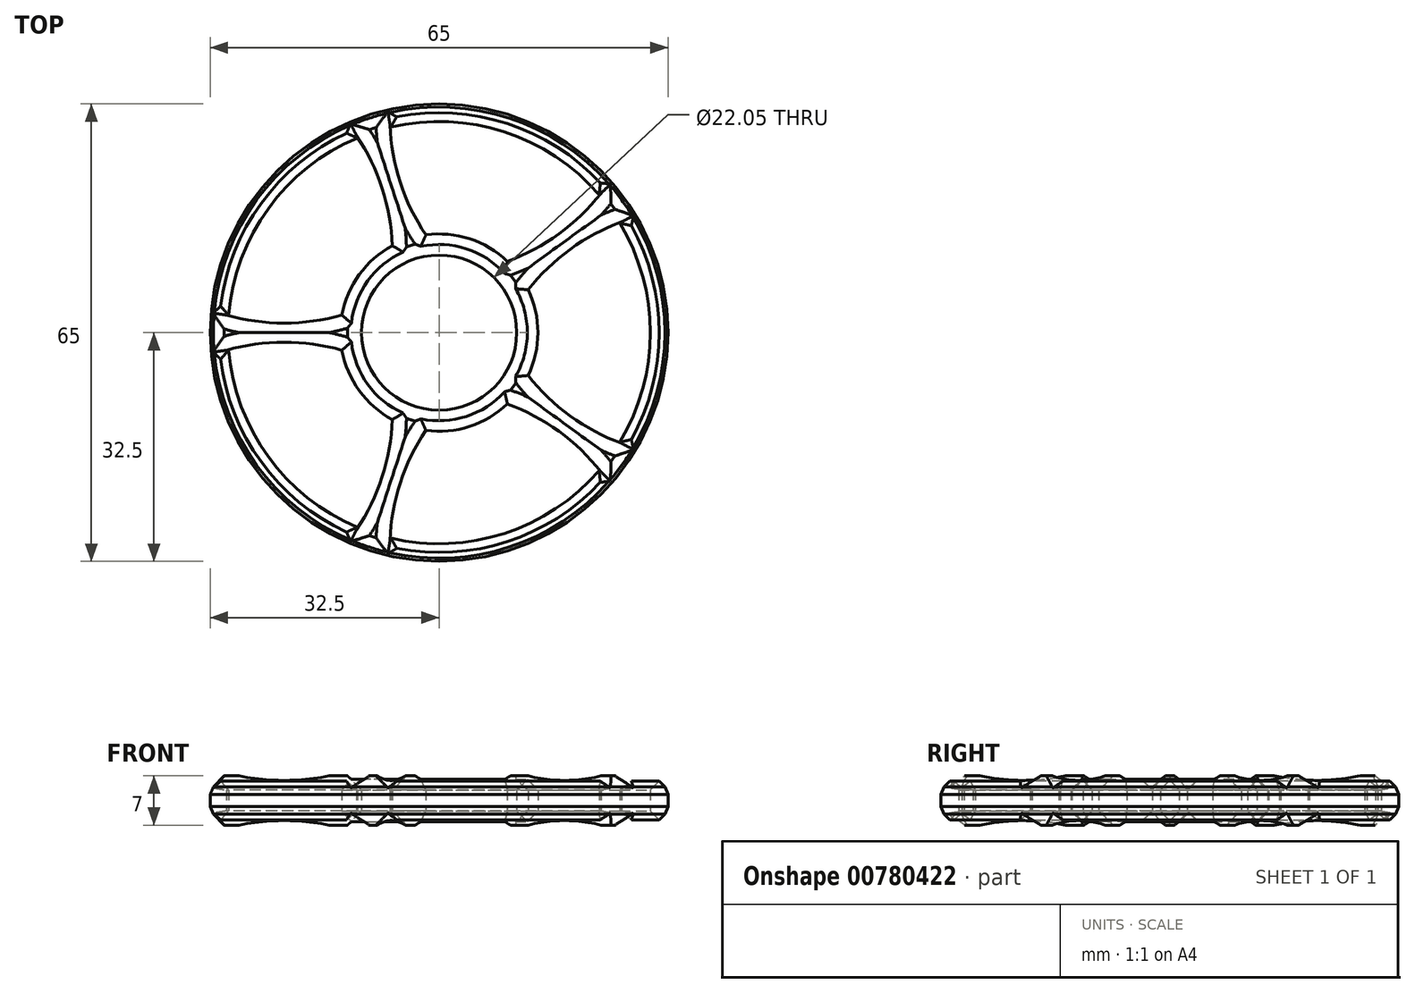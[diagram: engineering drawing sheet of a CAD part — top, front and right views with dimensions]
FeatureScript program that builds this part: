
annotation { "Feature Type Name" : "Feature", "Feature Type Description" : "" }
export const myFeature = defineFeature(function(context is Context, id is Id, definition is map)
    precondition{}
    {
        {
            var Q0;
            Q0=qCreatedBy(makeId("Top.planeOp"),FACE);
            var sketch = newSketch(context, id + "F0", { "sketchPlane" : qUnion([Q0])});
            skCircle(sketch, "E0", {"center": v(0, 0) * mm, "radius": 11.03 * mm});
            skCircle(sketch, "E1.0", {"center": v(0, 0) * mm, "radius": 14.02 * mm});
            skCircle(sketch, "E2", {"center": v(0, 0) * mm, "radius": 30 * mm});
            skLineSegment(sketch, "E3", {"start": v(-14.02, 0) * mm, "end": v(-30, 0) * mm});
            skCircle(sketch, "E4", {"center": v(0, 0) * mm, "radius": 32.5 * mm});
            skLineSegment(sketch, "E5.bottom", {"start": v(-13.8, -2.5) * mm, "end": v(-30.22, -2.5) * mm});
            skLineSegment(sketch, "E5.top", {"start": v(-13.8, 2.5) * mm, "end": v(-30.22, 2.5) * mm});
            skLineSegment(sketch, "E5.left", {"start": v(-13.8, -2.5) * mm, "end": v(-13.8, 2.5) * mm});
            skLineSegment(sketch, "E5.right", {"start": v(-30.22, -2.5) * mm, "end": v(-30.22, 2.5) * mm});
            skPoint(sketch, "E5.middle", {"position": v(-22.01, 0) * mm});
            skArc(sketch, "E6", {"start": v(-30.22, 2.5) * mm, "mid": v(-22.01, 1.35) * mm, "end": v(-13.8, 2.5) * mm});
            skArc(sketch, "E7", {"start": v(-13.8, -2.5) * mm, "mid": v(-22.01, -1.35) * mm, "end": v(-30.22, -2.5) * mm});
            skLineSegment(sketch, "E8.1.0", {"start": v(-6.64, -12.35) * mm, "end": v(-11.72, -27.97) * mm});
            skArc(sketch, "E8.1.1", {"start": v(-11.72, -27.97) * mm, "mid": v(-8.09, -20.52) * mm, "end": v(-6.64, -12.35) * mm});
            skLineSegment(sketch, "E8.1.2", {"start": v(-4.33, -13.34) * mm, "end": v(-9.27, -28.53) * mm});
            skArc(sketch, "E8.1.3", {"start": v(-1.89, -13.9) * mm, "mid": v(-5.51, -21.35) * mm, "end": v(-6.96, -29.52) * mm});
            skLineSegment(sketch, "E8.1.4", {"start": v(-1.89, -13.9) * mm, "end": v(-6.96, -29.52) * mm});
            skLineSegment(sketch, "E8.2.0", {"start": v(9.7, -10.13) * mm, "end": v(22.98, -19.79) * mm});
            skArc(sketch, "E8.2.1", {"start": v(22.98, -19.79) * mm, "mid": v(17.01, -14.03) * mm, "end": v(9.7, -10.13) * mm});
            skLineSegment(sketch, "E8.2.2", {"start": v(11.35, -8.24) * mm, "end": v(24.27, -17.63) * mm});
            skArc(sketch, "E8.2.3", {"start": v(12.63, -6.09) * mm, "mid": v(18.6, -11.84) * mm, "end": v(25.92, -15.74) * mm});
            skLineSegment(sketch, "E8.2.4", {"start": v(12.63, -6.09) * mm, "end": v(25.92, -15.74) * mm});
            skLineSegment(sketch, "E8.3.0", {"start": v(12.63, 6.09) * mm, "end": v(25.92, 15.74) * mm});
            skArc(sketch, "E8.3.1", {"start": v(25.92, 15.74) * mm, "mid": v(18.6, 11.84) * mm, "end": v(12.63, 6.09) * mm});
            skLineSegment(sketch, "E8.3.2", {"start": v(11.35, 8.24) * mm, "end": v(24.27, 17.63) * mm});
            skArc(sketch, "E8.3.3", {"start": v(9.7, 10.13) * mm, "mid": v(17.01, 14.03) * mm, "end": v(22.98, 19.79) * mm});
            skLineSegment(sketch, "E8.3.4", {"start": v(9.7, 10.13) * mm, "end": v(22.98, 19.79) * mm});
            skLineSegment(sketch, "E8.4.0", {"start": v(-1.89, 13.9) * mm, "end": v(-6.96, 29.52) * mm});
            skArc(sketch, "E8.4.1", {"start": v(-6.96, 29.52) * mm, "mid": v(-5.51, 21.35) * mm, "end": v(-1.89, 13.9) * mm});
            skLineSegment(sketch, "E8.4.2", {"start": v(-4.33, 13.34) * mm, "end": v(-9.27, 28.53) * mm});
            skArc(sketch, "E8.4.3", {"start": v(-6.64, 12.35) * mm, "mid": v(-8.09, 20.52) * mm, "end": v(-11.72, 27.97) * mm});
            skLineSegment(sketch, "E8.4.4", {"start": v(-6.64, 12.35) * mm, "end": v(-11.72, 27.97) * mm});
            skSolve(sketch);
        }
        {
            var Q0;
            Q0=makeQuery(id+"F0.imprint","IMPRINT",FACE,{"disambiguationData":[TD([[makeQuery(id+"F0.imprint","IMPRINT",EDGE,{"derivedFrom":sQuery(id+"F0.wireOp",EDGE,"E4")}),1.0]])]});
            var Q1;
            {var subQ3=sQuery(id+"F0.wireOp",EDGE,"E8.1.2");Q1=makeQuery(id+"F0.imprint","IMPRINT",FACE,{"disambiguationData":[TD([[makeQuery(id+"F0.imprint","IMPRINT",EDGE,{"derivedFrom":subQ3}),-1.0]])]});}
            var Q2;
            {var subQ0=sQuery(id+"F0.wireOp",EDGE,"E8.1.2");Q2=makeQuery(id+"F0.imprint","IMPRINT",FACE,{"disambiguationData":[TD([[makeQuery(id+"F0.imprint","IMPRINT",EDGE,{"derivedFrom":subQ0}),1.0]])]});}
            var Q3;
            {var subQ3=sQuery(id+"F0.wireOp",EDGE,"E8.2.2");Q3=makeQuery(id+"F0.imprint","IMPRINT",FACE,{"disambiguationData":[TD([[makeQuery(id+"F0.imprint","IMPRINT",EDGE,{"derivedFrom":subQ3}),-1.0]])]});}
            var Q4;
            {var subQ0=sQuery(id+"F0.wireOp",EDGE,"E8.2.2");Q4=makeQuery(id+"F0.imprint","IMPRINT",FACE,{"disambiguationData":[TD([[makeQuery(id+"F0.imprint","IMPRINT",EDGE,{"derivedFrom":subQ0}),1.0]])]});}
            var Q5;
            {var subQ3=sQuery(id+"F0.wireOp",EDGE,"E8.3.2");Q5=makeQuery(id+"F0.imprint","IMPRINT",FACE,{"disambiguationData":[TD([[makeQuery(id+"F0.imprint","IMPRINT",EDGE,{"derivedFrom":subQ3}),-1.0]])]});}
            var Q6;
            {var subQ0=sQuery(id+"F0.wireOp",EDGE,"E8.3.2");Q6=makeQuery(id+"F0.imprint","IMPRINT",FACE,{"disambiguationData":[TD([[makeQuery(id+"F0.imprint","IMPRINT",EDGE,{"derivedFrom":subQ0}),1.0]])]});}
            var Q7;
            {var subQ0=sQuery(id+"F0.wireOp",EDGE,"E8.4.2");Q7=makeQuery(id+"F0.imprint","IMPRINT",FACE,{"disambiguationData":[TD([[makeQuery(id+"F0.imprint","IMPRINT",EDGE,{"derivedFrom":subQ0}),1.0]])]});}
            var Q8;
            {var subQ3=sQuery(id+"F0.wireOp",EDGE,"E8.4.2");Q8=makeQuery(id+"F0.imprint","IMPRINT",FACE,{"disambiguationData":[TD([[makeQuery(id+"F0.imprint","IMPRINT",EDGE,{"derivedFrom":subQ3}),-1.0]])]});}
            var Q9;
            {var subQ3=sQuery(id+"F0.wireOp",EDGE,"E8.5.2");Q9=makeQuery(id+"F0.imprint","IMPRINT",FACE,{"disambiguationData":[TD([[makeQuery(id+"F0.imprint","IMPRINT",EDGE,{"derivedFrom":subQ3}),-1.0]])]});}
            var Q10;
            {var subQ0=sQuery(id+"F0.wireOp",EDGE,"E8.5.2");Q10=makeQuery(id+"F0.imprint","IMPRINT",FACE,{"disambiguationData":[TD([[makeQuery(id+"F0.imprint","IMPRINT",EDGE,{"derivedFrom":subQ0}),1.0]])]});}
            var Q11;
            Q11=makeQuery(id+"F0.imprint","IMPRINT",FACE,{"disambiguationData":[TD([[makeQuery(id+"F0.imprint","IMPRINT",EDGE,{"derivedFrom":sQuery(id+"F0.wireOp",EDGE,"E0")}),-1.0]])]});
            var Q12;
            {var subQ3=sQuery(id+"F0.wireOp",EDGE,"E8.6.2");Q12=makeQuery(id+"F0.imprint","IMPRINT",FACE,{"disambiguationData":[TD([[makeQuery(id+"F0.imprint","IMPRINT",EDGE,{"derivedFrom":subQ3}),-1.0]])]});}
            var Q13;
            {var subQ0=sQuery(id+"F0.wireOp",EDGE,"E8.6.2");Q13=makeQuery(id+"F0.imprint","IMPRINT",FACE,{"disambiguationData":[TD([[makeQuery(id+"F0.imprint","IMPRINT",EDGE,{"derivedFrom":subQ0}),1.0]])]});}
            var Q14;
            {var subQ0=sQuery(id+"F0.wireOp",EDGE,"E3");Q14=makeQuery(id+"F0.imprint","IMPRINT",FACE,{"disambiguationData":[TD([[makeQuery(id+"F0.imprint","IMPRINT",EDGE,{"derivedFrom":subQ0}),-1.0]])]});}
            var Q15;
            {var subQ0=sQuery(id+"F0.wireOp",EDGE,"E3");Q15=makeQuery(id+"F0.imprint","IMPRINT",FACE,{"disambiguationData":[TD([[makeQuery(id+"F0.imprint","IMPRINT",EDGE,{"derivedFrom":subQ0}),1.0]])]});}
            var Q16;
            {var subQ2=sQuery(id+"F0.wireOp",EDGE,"E5.left");Q16=makeQuery(id+"F0.imprint","IMPRINT",FACE,{"disambiguationData":[TD([[makeQuery(id+"F0.imprint","IMPRINT",EDGE,{"derivedFrom":subQ2}),1.0]])]});}
            var Q17;
            {var subQ1=sQuery(id+"F0.wireOp",EDGE,"E5.right");Q17=makeQuery(id+"F0.imprint","IMPRINT",FACE,{"disambiguationData":[TD([[makeQuery(id+"F0.imprint","IMPRINT",EDGE,{"derivedFrom":subQ1}),-1.0]])]});}
            extrude(context, id + "F1", {"entities" : qUnion([Q0, Q1, Q2, Q3, Q4, Q5, Q6, Q7, Q8, Q9, Q10, Q11, Q12, Q13, Q14, Q15, Q16, Q17]), "depth" : 7 * mm, "offsetDistance" : 25 * mm});
        }
        {
            var Q0;
            Q0=makeQuery(id+"F1.opExtrude","CAP_FACE",FACE,{"disambiguationData":[OSD([sQuery(id+"F0.wireOp",EDGE,"E0"),sQuery(id+"F0.wireOp",EDGE,"E1.0"),sQuery(id+"F0.wireOp",EDGE,"E2"),sQuery(id+"F0.wireOp",EDGE,"E4"),sQuery(id+"F0.wireOp",EDGE,"E5.bottom"),sQuery(id+"F0.wireOp",EDGE,"E5.top"),sQuery(id+"F0.wireOp",EDGE,"E6"),sQuery(id+"F0.wireOp",EDGE,"E7"),sQuery(id+"F0.wireOp",EDGE,"E8.1.0"),sQuery(id+"F0.wireOp",EDGE,"E8.1.1"),sQuery(id+"F0.wireOp",EDGE,"E8.1.3"),sQuery(id+"F0.wireOp",EDGE,"E8.1.4"),sQuery(id+"F0.wireOp",EDGE,"E8.2.0"),sQuery(id+"F0.wireOp",EDGE,"E8.2.1"),sQuery(id+"F0.wireOp",EDGE,"E8.2.3"),sQuery(id+"F0.wireOp",EDGE,"E8.2.4"),sQuery(id+"F0.wireOp",EDGE,"E8.3.0"),sQuery(id+"F0.wireOp",EDGE,"E8.3.1"),sQuery(id+"F0.wireOp",EDGE,"E8.3.3"),sQuery(id+"F0.wireOp",EDGE,"E8.3.4"),sQuery(id+"F0.wireOp",EDGE,"E8.4.0"),sQuery(id+"F0.wireOp",EDGE,"E8.4.1"),sQuery(id+"F0.wireOp",EDGE,"E8.4.3"),sQuery(id+"F0.wireOp",EDGE,"E8.4.4"),sQuery(id+"F0.wireOp",EDGE,"E8.5.0"),sQuery(id+"F0.wireOp",EDGE,"E8.5.1"),sQuery(id+"F0.wireOp",EDGE,"E8.5.3"),sQuery(id+"F0.wireOp",EDGE,"E8.5.4"),sQuery(id+"F0.wireOp",EDGE,"E8.6.0"),sQuery(id+"F0.wireOp",EDGE,"E8.6.1"),sQuery(id+"F0.wireOp",EDGE,"E8.6.3"),sQuery(id+"F0.wireOp",EDGE,"E8.6.4")])],"isStart":false});
            var Q1;
            Q1=makeQuery(id+"F1.opExtrude","CAP_FACE",FACE,{"disambiguationData":[OSD([sQuery(id+"F0.wireOp",EDGE,"E0"),sQuery(id+"F0.wireOp",EDGE,"E1.0"),sQuery(id+"F0.wireOp",EDGE,"E2"),sQuery(id+"F0.wireOp",EDGE,"E4"),sQuery(id+"F0.wireOp",EDGE,"E5.bottom"),sQuery(id+"F0.wireOp",EDGE,"E5.top"),sQuery(id+"F0.wireOp",EDGE,"E6"),sQuery(id+"F0.wireOp",EDGE,"E7"),sQuery(id+"F0.wireOp",EDGE,"E8.1.0"),sQuery(id+"F0.wireOp",EDGE,"E8.1.1"),sQuery(id+"F0.wireOp",EDGE,"E8.1.3"),sQuery(id+"F0.wireOp",EDGE,"E8.1.4"),sQuery(id+"F0.wireOp",EDGE,"E8.2.0"),sQuery(id+"F0.wireOp",EDGE,"E8.2.1"),sQuery(id+"F0.wireOp",EDGE,"E8.2.3"),sQuery(id+"F0.wireOp",EDGE,"E8.2.4"),sQuery(id+"F0.wireOp",EDGE,"E8.3.0"),sQuery(id+"F0.wireOp",EDGE,"E8.3.1"),sQuery(id+"F0.wireOp",EDGE,"E8.3.3"),sQuery(id+"F0.wireOp",EDGE,"E8.3.4"),sQuery(id+"F0.wireOp",EDGE,"E8.4.0"),sQuery(id+"F0.wireOp",EDGE,"E8.4.1"),sQuery(id+"F0.wireOp",EDGE,"E8.4.3"),sQuery(id+"F0.wireOp",EDGE,"E8.4.4"),sQuery(id+"F0.wireOp",EDGE,"E8.5.0"),sQuery(id+"F0.wireOp",EDGE,"E8.5.1"),sQuery(id+"F0.wireOp",EDGE,"E8.5.3"),sQuery(id+"F0.wireOp",EDGE,"E8.5.4"),sQuery(id+"F0.wireOp",EDGE,"E8.6.0"),sQuery(id+"F0.wireOp",EDGE,"E8.6.1"),sQuery(id+"F0.wireOp",EDGE,"E8.6.3"),sQuery(id+"F0.wireOp",EDGE,"E8.6.4")])],"isStart":true});
            chamfer(context, id + "F2", {"entities" : qUnion([Q0, Q1]), "width" : 2 * mm, "tangentPropagation" : true});
        }
        {
            var Q0;
            Q0=makeQuery(id+"F1.opExtrude","SWEPT_FACE",FACE,{"disambiguationData":[OSD([sQuery(id+"F0.wireOp",EDGE,"E4")])]});
            chamfer(context, id + "F3", {"entities" : qUnion([Q0]), "width" : 1.5 * mm, "tangentPropagation" : true});
        }
    });
